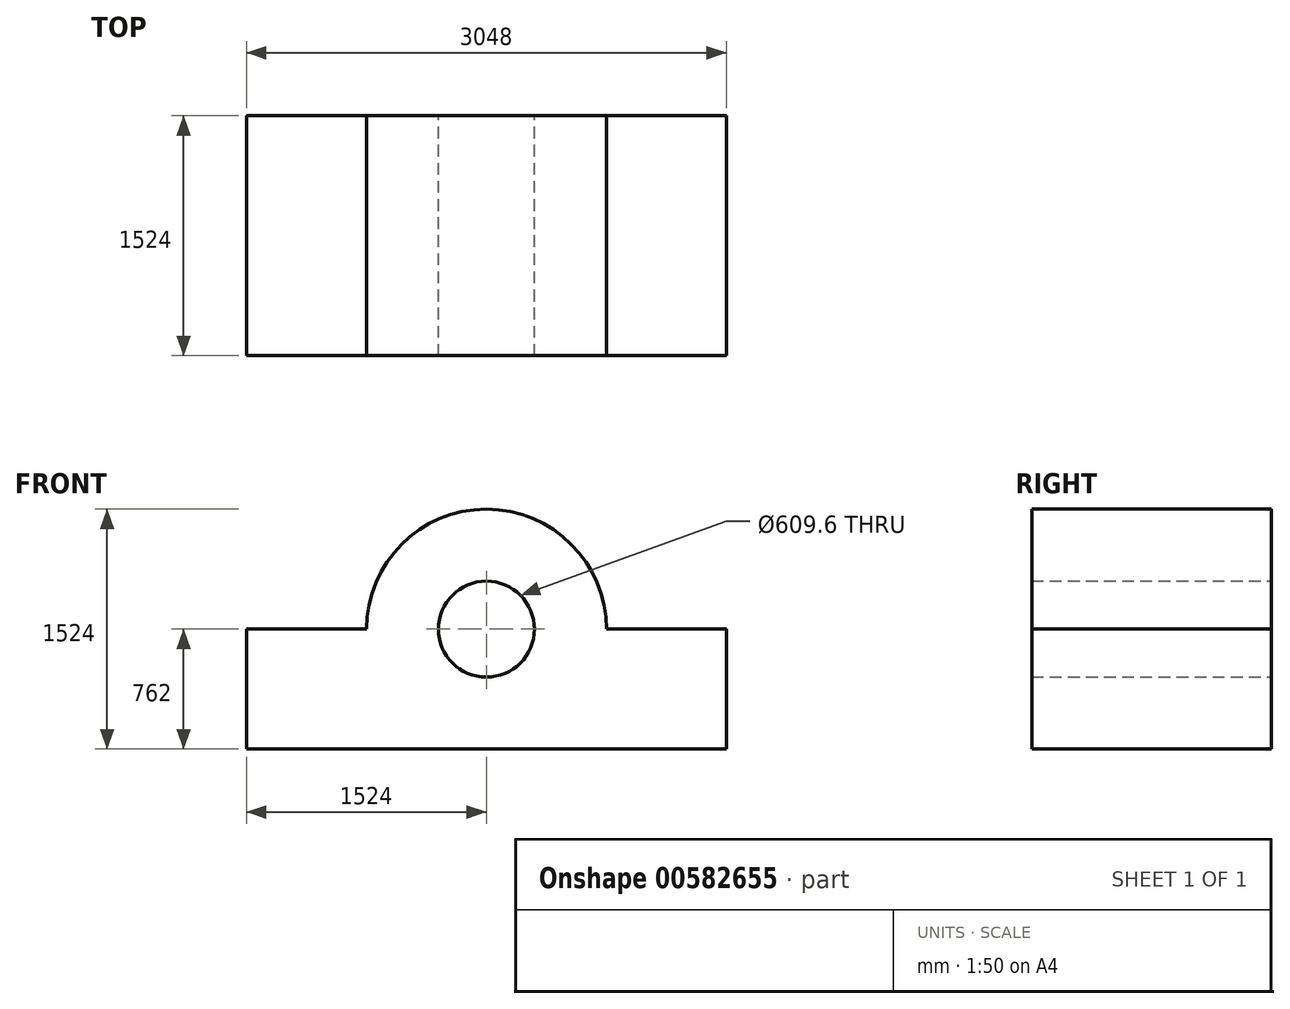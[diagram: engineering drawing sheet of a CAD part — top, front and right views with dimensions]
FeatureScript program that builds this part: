
annotation { "Feature Type Name" : "Feature", "Feature Type Description" : "" }
export const myFeature = defineFeature(function(context is Context, id is Id, definition is map)
    precondition{}
    {
        {
            var Q0;
            Q0=qCreatedBy(makeId("Front.planeOp"),FACE);
            var sketch = newSketch(context, id + "F0", { "sketchPlane" : qUnion([Q0])});
            skLineSegment(sketch, "E0", {"start": v(0, 0) * mm, "end": v(0, 762) * mm});
            skLineSegment(sketch, "E1", {"start": v(0, 0) * mm, "end": v(-3048, 0) * mm});
            skLineSegment(sketch, "E2", {"start": v(-3048, 0) * mm, "end": v(-3048, 762) * mm});
            skArc(sketch, "E3", {"start": v(-762, 762) * mm, "mid": v(-1524, 1524) * mm, "end": v(-2286, 762) * mm});
            skPoint(sketch, "E3.centerSnap0", {"position": v(-1524, 0) * mm});
            skLineSegment(sketch, "E4", {"start": v(-3048, 762) * mm, "end": v(-2286, 762) * mm});
            skLineSegment(sketch, "E5", {"start": v(0, 762) * mm, "end": v(-762, 762) * mm});
            skCircle(sketch, "E6", {"center": v(-1524, 762) * mm, "radius": 304.8 * mm});
            skSolve(sketch);
        }
        {
            var Q0;
            Q0=makeQuery(id+"F0.imprint","IMPRINT",FACE,{"disambiguationData":[TD([[makeQuery(id+"F0.imprint","IMPRINT",EDGE,{"derivedFrom":sQuery(id+"F0.wireOp",EDGE,"E0")}),1.0]])]});
            extrude(context, id + "F1", {"entities" : qUnion([Q0]), "depth" : 1524 * mm, "offsetDistance" : 25.4 * mm});
        }
    });
